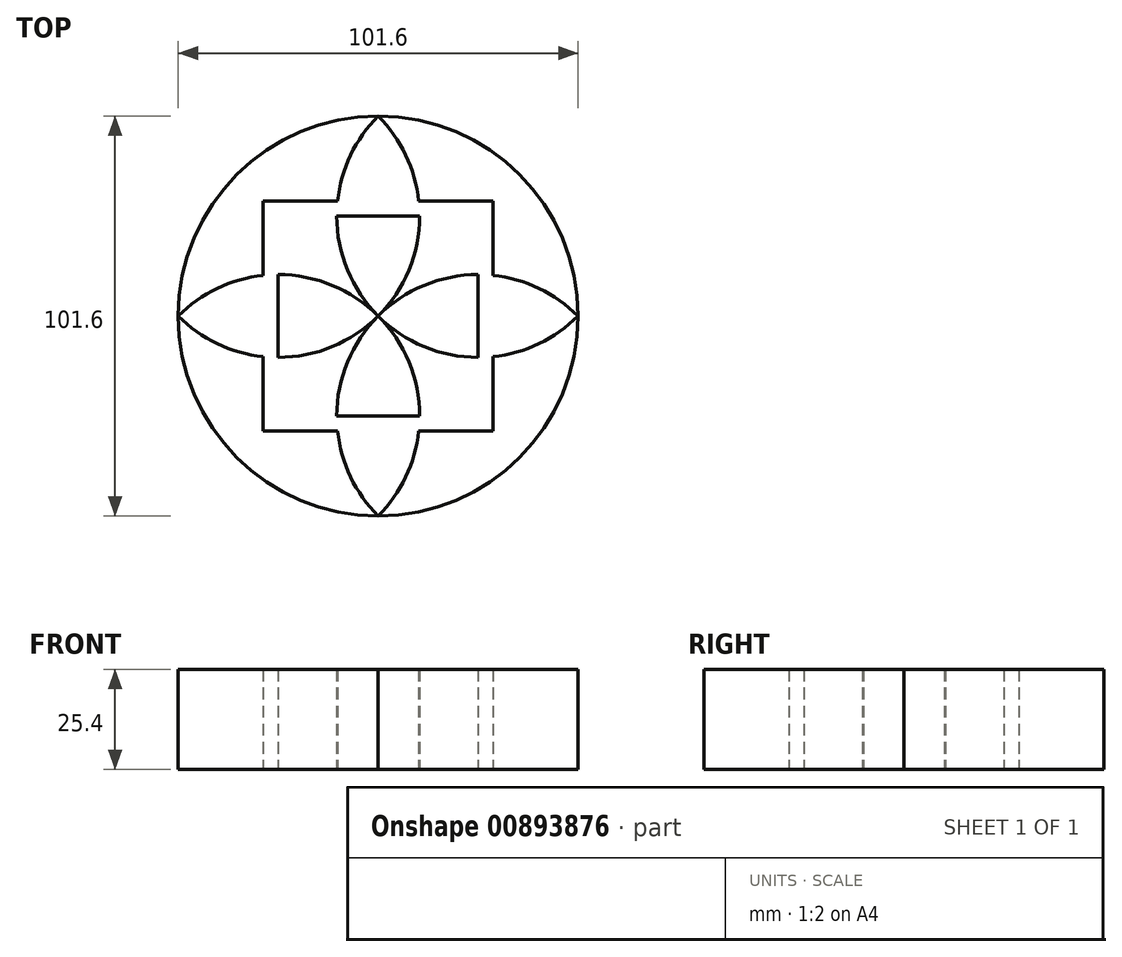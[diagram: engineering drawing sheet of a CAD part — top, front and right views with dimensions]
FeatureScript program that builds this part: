
annotation { "Feature Type Name" : "Feature", "Feature Type Description" : "" }
export const myFeature = defineFeature(function(context is Context, id is Id, definition is map)
    precondition{}
    {
        {
            var Q0;
            Q0=qCreatedBy(makeId("Top.planeOp"),FACE);
            var sketch = newSketch(context, id + "F0", { "sketchPlane" : qUnion([Q0])});
            skLineSegment(sketch, "E0.bottom", {"start": v(0, 50.8) * mm, "end": v(0, 50.8) * mm});
            skLineSegment(sketch, "E0.top", {"start": v(0, -50.8) * mm, "end": v(0, -50.8) * mm});
            skLineSegment(sketch, "E0.left", {"start": v(-50.8, 0) * mm, "end": v(-50.8, 0) * mm});
            skLineSegment(sketch, "E0.right", {"start": v(50.8, 0) * mm, "end": v(50.8, 0) * mm});
            skPoint(sketch, "E0.middle", {"position": v(0, 0) * mm});
            skPoint(sketch, "E1.visualSharp", {"position": v(-50.8, 50.8) * mm});
            skArc(sketch, "E1.filletArc", {"start": v(0, 50.8) * mm, "mid": v(-35.92, 35.92) * mm, "end": v(-50.8, 0) * mm});
            skPoint(sketch, "E2.visualSharp", {"position": v(-50.8, -50.8) * mm});
            skArc(sketch, "E2.filletArc", {"start": v(-50.8, 0) * mm, "mid": v(-35.92, -35.92) * mm, "end": v(0, -50.8) * mm});
            skPoint(sketch, "E3.visualSharp", {"position": v(50.8, -50.8) * mm});
            skArc(sketch, "E3.filletArc", {"start": v(0, -50.8) * mm, "mid": v(35.92, -35.92) * mm, "end": v(50.8, 0) * mm});
            skPoint(sketch, "E4.visualSharp", {"position": v(50.8, 50.8) * mm});
            skArc(sketch, "E4.filletArc", {"start": v(50.8, 0) * mm, "mid": v(35.92, 35.92) * mm, "end": v(0, 50.8) * mm});
            skArc(sketch, "E5", {"start": v(0, 50.8) * mm, "mid": v(0, 0) * mm, "end": v(50.8, 0) * mm});
            skArc(sketch, "E6", {"start": v(-50.8, 0) * mm, "mid": v(0, 0) * mm, "end": v(0, 50.8) * mm});
            skArc(sketch, "E7", {"start": v(0, -50.8) * mm, "mid": v(0, 0) * mm, "end": v(-50.8, 0) * mm});
            skArc(sketch, "E8", {"start": v(50.8, 0) * mm, "mid": v(0, 0) * mm, "end": v(0, -50.8) * mm});
            skLineSegment(sketch, "E9.bottom", {"start": v(-25.4, 25.4) * mm, "end": v(25.4, 25.4) * mm});
            skLineSegment(sketch, "E9.top", {"start": v(-25.4, -25.4) * mm, "end": v(25.4, -25.4) * mm});
            skLineSegment(sketch, "E9.left", {"start": v(-25.4, 25.4) * mm, "end": v(-25.4, -25.4) * mm});
            skLineSegment(sketch, "E9.right", {"start": v(25.4, 25.4) * mm, "end": v(25.4, -25.4) * mm});
            skLineSegment(sketch, "E10.0", {"start": v(-29.21, 29.21) * mm, "end": v(29.21, 29.21) * mm});
            skLineSegment(sketch, "E10.1", {"start": v(-29.21, 29.21) * mm, "end": v(-29.21, -29.21) * mm});
            skLineSegment(sketch, "E10.2", {"start": v(-29.21, -29.21) * mm, "end": v(29.21, -29.21) * mm});
            skLineSegment(sketch, "E10.3", {"start": v(29.21, 29.21) * mm, "end": v(29.21, -29.21) * mm});
            skSolve(sketch);
        }
        {
            var Q0;
            {var subQ2=sQuery(id+"F0.wireOp",EDGE,"E1.filletArc");Q0=makeQuery(id+"F0.imprint","IMPRINT",FACE,{"disambiguationData":[TD([[makeQuery(id+"F0.imprint","IMPRINT",EDGE,{"derivedFrom":subQ2}),1.0]])]});}
            var Q1;
            {var subQ7=sQuery(id+"F0.wireOp",EDGE,"E4.filletArc");Q1=makeQuery(id+"F0.imprint","IMPRINT",FACE,{"disambiguationData":[TD([[makeQuery(id+"F0.imprint","IMPRINT",EDGE,{"derivedFrom":subQ7}),1.0]])]});}
            var Q2;
            {var subQ6=sQuery(id+"F0.wireOp",EDGE,"E3.filletArc");Q2=makeQuery(id+"F0.imprint","IMPRINT",FACE,{"disambiguationData":[TD([[makeQuery(id+"F0.imprint","IMPRINT",EDGE,{"derivedFrom":subQ6}),1.0]])]});}
            var Q3;
            {var subQ2=sQuery(id+"F0.wireOp",EDGE,"E2.filletArc");Q3=makeQuery(id+"F0.imprint","IMPRINT",FACE,{"disambiguationData":[TD([[makeQuery(id+"F0.imprint","IMPRINT",EDGE,{"derivedFrom":subQ2}),1.0]])]});}
            var Q4;
            {var subQ0=sQuery(id+"F0.wireOp",EDGE,"E9.left");var subQ1=sQuery(id+"F0.wireOp",EDGE,"E6");var subQ2=makeQuery(id+"F0.imprint","INTERSECT",VERTEX,{"derivedFrom":[subQ1,subQ0]});Q4=makeQuery(id+"F0.imprint","IMPRINT",FACE,{"disambiguationData":[TD([[makeQuery(id+"F0.imprint","IMPRINT",EDGE,{"disambiguationData":[TD([[subQ2,1.0]])],"derivedFrom":subQ0}),1.0]])]});}
            var Q5;
            {var subQ0=sQuery(id+"F0.wireOp",EDGE,"E9.bottom");var subQ1=sQuery(id+"F0.wireOp",EDGE,"E5");var subQ2=makeQuery(id+"F0.imprint","INTERSECT",VERTEX,{"derivedFrom":[subQ1,subQ0]});Q5=makeQuery(id+"F0.imprint","IMPRINT",FACE,{"disambiguationData":[TD([[makeQuery(id+"F0.imprint","IMPRINT",EDGE,{"disambiguationData":[TD([[subQ2,-1.0]])],"derivedFrom":subQ0}),-1.0]])]});}
            var Q6;
            {var subQ0=sQuery(id+"F0.wireOp",EDGE,"E9.right");var subQ1=sQuery(id+"F0.wireOp",EDGE,"E5");var subQ2=makeQuery(id+"F0.imprint","INTERSECT",VERTEX,{"derivedFrom":[subQ1,subQ0]});Q6=makeQuery(id+"F0.imprint","IMPRINT",FACE,{"disambiguationData":[TD([[makeQuery(id+"F0.imprint","IMPRINT",EDGE,{"disambiguationData":[TD([[subQ2,1.0]])],"derivedFrom":subQ0}),-1.0]])]});}
            var Q7;
            {var subQ0=sQuery(id+"F0.wireOp",EDGE,"E9.top");var subQ1=sQuery(id+"F0.wireOp",EDGE,"E7");var subQ2=makeQuery(id+"F0.imprint","INTERSECT",VERTEX,{"derivedFrom":[subQ1,subQ0]});Q7=makeQuery(id+"F0.imprint","IMPRINT",FACE,{"disambiguationData":[TD([[makeQuery(id+"F0.imprint","IMPRINT",EDGE,{"disambiguationData":[TD([[subQ2,1.0]])],"derivedFrom":subQ0}),1.0]])]});}
            extrude(context, id + "F1", {"entities" : qUnion([Q0, Q1, Q2, Q3, Q4, Q5, Q6, Q7]), "depth" : 25.4 * mm, "offsetDistance" : 25.4 * mm});
        }
    });
